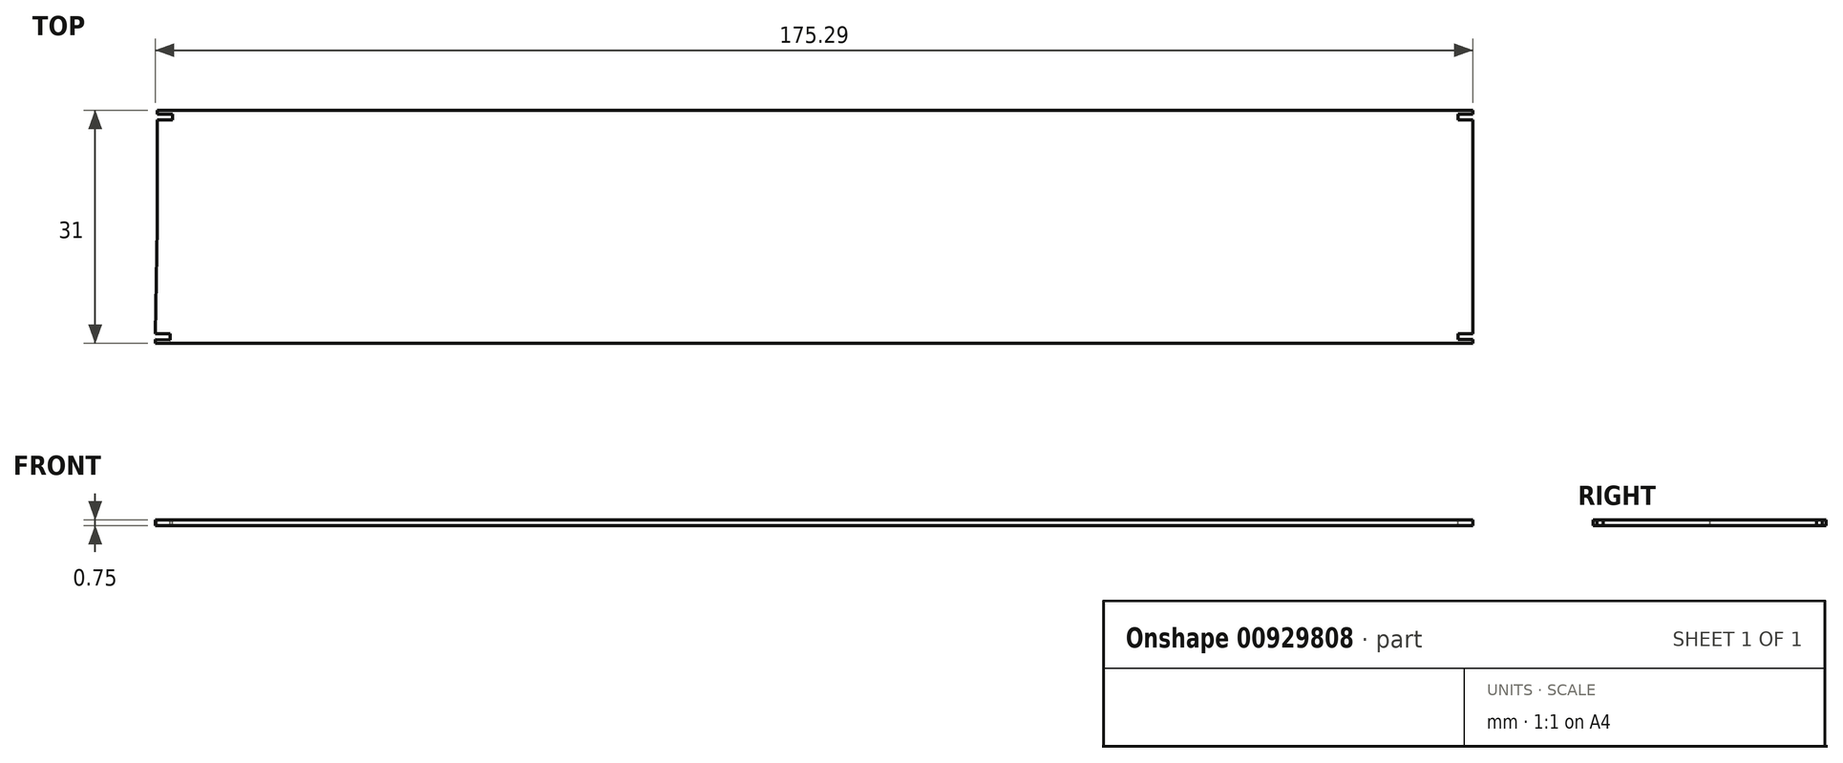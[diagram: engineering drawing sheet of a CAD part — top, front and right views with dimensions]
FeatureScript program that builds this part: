
annotation { "Feature Type Name" : "Feature", "Feature Type Description" : "" }
export const myFeature = defineFeature(function(context is Context, id is Id, definition is map)
    precondition{}
    {
        {
            var Q0;
            Q0=qCreatedBy(makeId("Top.planeOp"),FACE);
            var sketch = newSketch(context, id + "F0", { "sketchPlane" : qUnion([Q0])});
            skLineSegment(sketch, "E0", {"start": v(-87.52, 0) * mm, "end": v(-87.52, 15.5) * mm});
            skLineSegment(sketch, "E1", {"start": v(-87.52, 15.5) * mm, "end": v(87.48, 15.5) * mm});
            skLineSegment(sketch, "E2", {"start": v(87.48, 15.5) * mm, "end": v(87.48, -15.5) * mm});
            skLineSegment(sketch, "E3", {"start": v(87.48, -15.5) * mm, "end": v(-87.81, -15.5) * mm});
            skLineSegment(sketch, "E4", {"start": v(-87.81, -15.5) * mm, "end": v(-87.52, 0) * mm});
            skSolve(sketch);
        }
        {
            var Q0;
            Q0=makeQuery(id+"F0.imprint","IMPRINT",FACE,{"disambiguationData":[TD([[makeQuery(id+"F0.imprint","IMPRINT",EDGE,{"derivedFrom":sQuery(id+"F0.wireOp",EDGE,"E0")}),-1.0]])]});
            extrude(context, id + "F1", {"entities" : qUnion([Q0]), "depth" : .75 * mm, "offsetDistance" : 25.4 * mm});
        }
        {
            var Q0;
            Q0=makeQuery(id+"F1.opExtrude","CAP_FACE",FACE,{"disambiguationData":[OSD([sQuery(id+"F0.wireOp",EDGE,"E0"),sQuery(id+"F0.wireOp",EDGE,"E1"),sQuery(id+"F0.wireOp",EDGE,"E2"),sQuery(id+"F0.wireOp",EDGE,"E3"),sQuery(id+"F0.wireOp",EDGE,"E4")])],"isStart":false});
            var sketch = newSketch(context, id + "F2", { "sketchPlane" : qUnion([Q0])});
            skLineSegment(sketch, "E5", {"start": v(-87.8, -15) * mm, "end": v(-85.8, -15.04) * mm});
            skLineSegment(sketch, "E6", {"start": v(-85.8, -15.04) * mm, "end": v(-85.8, -14.24) * mm});
            skLineSegment(sketch, "E7", {"start": v(-85.8, -14.24) * mm, "end": v(-87.81, -14.24) * mm});
            skSolve(sketch);
        }
        {
            var Q0;
            Q0 = qSketchRegion(id + "F2", true);
            var Q1;
            {var subQ0=sQuery(id+"F2.wireOp",EDGE,"E5");Q1=makeQuery(id+"F2.imprint","IMPRINT",FACE,{"disambiguationData":[TD([[makeQuery(id+"F2.imprint","IMPRINT",EDGE,{"derivedFrom":subQ0}),1.0]])]});}
            extrude(context, id + "F3", {"entities" : qUnion([Q0, Q1]), "operationType" : NewBodyOperationType.REMOVE, "endBound" : BoundingType.UP_TO_NEXT, "oppositeDirection" : true, "depth" : 25 * mm, "offsetDistance" : 25 * mm});
        }
        {
            var Q0;
            Q0=makeQuery(id+"F1.opExtrude","CAP_FACE",FACE,{"disambiguationData":[OSD([sQuery(id+"F0.wireOp",EDGE,"E0"),sQuery(id+"F0.wireOp",EDGE,"E1"),sQuery(id+"F0.wireOp",EDGE,"E2"),sQuery(id+"F0.wireOp",EDGE,"E3"),sQuery(id+"F0.wireOp",EDGE,"E4")])],"isStart":false});
            var sketch = newSketch(context, id + "F4", { "sketchPlane" : qUnion([Q0])});
            skLineSegment(sketch, "E8", {"start": v(-87.52, 15) * mm, "end": v(-85.52, 15) * mm});
            skLineSegment(sketch, "E9", {"start": v(-85.52, 15) * mm, "end": v(-85.52, 14.2) * mm});
            skLineSegment(sketch, "E10", {"start": v(-85.52, 14.2) * mm, "end": v(-87.52, 14.2) * mm});
            skSolve(sketch);
        }
        {
            var Q0;
            Q0 = qSketchRegion(id + "F4", true);
            var Q1;
            {var subQ0=sQuery(id+"F4.wireOp",EDGE,"E8");Q1=makeQuery(id+"F4.imprint","IMPRINT",FACE,{"disambiguationData":[TD([[makeQuery(id+"F4.imprint","IMPRINT",EDGE,{"derivedFrom":subQ0}),-1.0]])]});}
            extrude(context, id + "F5", {"entities" : qUnion([Q0, Q1]), "operationType" : NewBodyOperationType.REMOVE, "oppositeDirection" : true, "depth" : 25 * mm, "offsetDistance" : 25 * mm});
        }
        {
            var Q0;
            Q0=makeQuery(id+"F1.opExtrude","CAP_FACE",FACE,{"disambiguationData":[OSD([sQuery(id+"F0.wireOp",EDGE,"E0"),sQuery(id+"F0.wireOp",EDGE,"E1"),sQuery(id+"F0.wireOp",EDGE,"E2"),sQuery(id+"F0.wireOp",EDGE,"E3"),sQuery(id+"F0.wireOp",EDGE,"E4")])],"isStart":false});
            var sketch = newSketch(context, id + "F6", { "sketchPlane" : qUnion([Q0])});
            skLineSegment(sketch, "E11", {"start": v(87.48, 15) * mm, "end": v(85.48, 15) * mm});
            skLineSegment(sketch, "E12", {"start": v(85.48, 15) * mm, "end": v(85.48, 14.2) * mm});
            skLineSegment(sketch, "E13", {"start": v(85.48, 14.2) * mm, "end": v(87.48, 14.2) * mm});
            skSolve(sketch);
        }
        {
            var Q0;
            {var subQ0=sQuery(id+"F6.wireOp",EDGE,"E11");Q0=makeQuery(id+"F6.imprint","IMPRINT",FACE,{"disambiguationData":[TD([[makeQuery(id+"F6.imprint","IMPRINT",EDGE,{"derivedFrom":subQ0}),1.0]])]});}
            extrude(context, id + "F7", {"entities" : qUnion([Q0]), "operationType" : NewBodyOperationType.REMOVE, "endBound" : BoundingType.THROUGH_ALL, "oppositeDirection" : true, "depth" : 25 * mm, "offsetDistance" : 25 * mm});
        }
        {
            var Q0;
            Q0=makeQuery(id+"F1.opExtrude","CAP_FACE",FACE,{"disambiguationData":[OSD([sQuery(id+"F0.wireOp",EDGE,"E0"),sQuery(id+"F0.wireOp",EDGE,"E1"),sQuery(id+"F0.wireOp",EDGE,"E2"),sQuery(id+"F0.wireOp",EDGE,"E3"),sQuery(id+"F0.wireOp",EDGE,"E4")])],"isStart":false});
            var sketch = newSketch(context, id + "F8", { "sketchPlane" : qUnion([Q0])});
            skLineSegment(sketch, "E14", {"start": v(87.48, -14.2) * mm, "end": v(85.48, -14.2) * mm});
            skLineSegment(sketch, "E15", {"start": v(85.48, -14.2) * mm, "end": v(85.48, -15) * mm});
            skLineSegment(sketch, "E16", {"start": v(85.48, -15) * mm, "end": v(87.48, -15) * mm});
            skSolve(sketch);
        }
        {
            var Q0;
            Q0 = qSketchRegion(id + "F8", true);
            var Q1;
            {var subQ0=sQuery(id+"F8.wireOp",EDGE,"E14");Q1=makeQuery(id+"F8.imprint","IMPRINT",FACE,{"disambiguationData":[TD([[makeQuery(id+"F8.imprint","IMPRINT",EDGE,{"derivedFrom":subQ0}),1.0]])]});}
            extrude(context, id + "F9", {"entities" : qUnion([Q0, Q1]), "operationType" : NewBodyOperationType.REMOVE, "endBound" : BoundingType.THROUGH_ALL, "oppositeDirection" : true, "depth" : 25 * mm, "offsetDistance" : 25 * mm});
        }
    });
